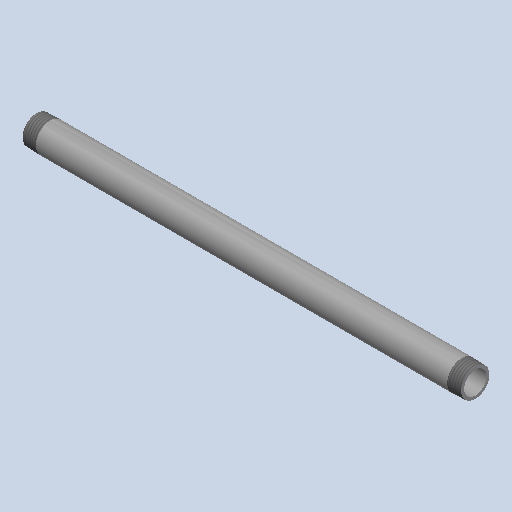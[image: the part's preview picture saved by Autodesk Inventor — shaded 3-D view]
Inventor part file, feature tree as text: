
AUTODESK INVENTOR PART (.ipt)
format: ipt  version: 2025 (Build 290162000, 162)  size: 160,768 bytes
history: native  units: mm (DEFAULTED — no unit token found)
features: other x8, revolve x1
ambient origin geometry x8: Origin, YZ Plane, XZ Plane, XY Plane, X Axis, Y Axis, Z Axis, Center Point
bodies: Solid1 (feature_tree)
feature tree (9):
  revolve  "Revolution1"  [1 undecoded]
  other  "Work Axis1"
  other  "Work Point5"
  other  "Work Axis2"
  other  "Work Point6"
  other  "Work Axis3"
  other  "Work Axis4"
  other  "Work Point7"
  other  "Work Point8"
note: 1 required parameter value undecoded (feature->parameter linkage not recoverable at this tier; creation-order binding heuristic only, values carry confidence <= 0.55)
